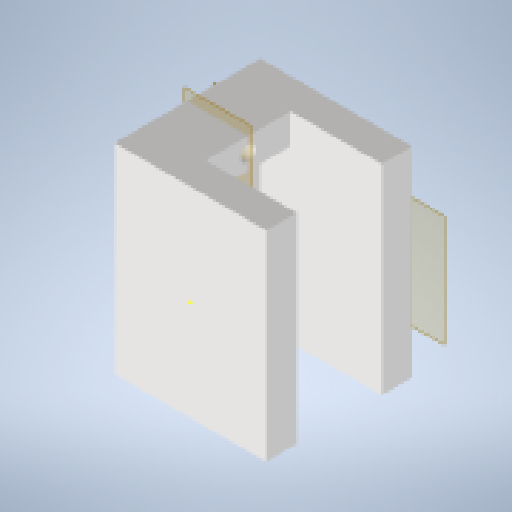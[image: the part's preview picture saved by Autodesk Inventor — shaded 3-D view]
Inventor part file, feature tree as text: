
AUTODESK INVENTOR PART (.ipt)
format: ipt  version: 2023.2 (Build 272271000, 271)  size: 275,456 bytes
history: native  units: mm
features: sketch x6, extrude x5, other x4, plane x2, mirror x1, reference x1, projected_geometry x1
ambient origin geometry x8: Origin, YZ Plane, XZ Plane, XY Plane, X Axis, Y Axis, Z Axis, Center Point
bodies: Solid1 (feature_tree)
feature tree (20):
  plane  "Work Plane1"
  extrude  "Extrusion1"  Depth=33.0mm
  extrude  "Extrusion2"  Depth=5.0mm
  extrude  "Extrusion3"  Depth=5.0mm
  sketch  "Sketch4"  dims[d8=5.0mm d9=2.5mm]
  extrude  "Extrusion4"  Depth=5.0mm
  plane  "Work Plane2"
  mirror  "Mirror1"
  extrude  "Extrusion5"  Depth=2.5mm
  sketch  "Sketch1"  dims[d0=25.0mm d1=33.0mm]
  reference  "Reference1"
  sketch  "Sketch2"  dims[d2=5.0mm d3=0.0mm d4=5.0mm]
  sketch  "Sketch3"  dims[d5=14.0mm d6=0.0mm d7=5.0mm]
  sketch  "Sketch5"  dims[d10=2.5mm d11=2.5mm]
  sketch  "Sketch6"  dims[d12=7.0mm d13=2.5mm d14=7.0mm d15=5.0mm d16=0.0mm d17=12.5mm d18=6.5mm d19=11.0mm d20=7.0mm d21=7.0mm d22=5.0mm d23=0.0mm d24=-7.0mm d25=2.0mm d26=0.0mm]
  projected_geometry  "Projected Loop1"
  other  "<userpath> windows\Documents\Inventor\Robotska_roka\Assembly4.iam"
  other  "Assembly4.iam"
  other  "SG90 - Micro Servo 9g - Tower Pro:2"
  other  "SG90 - Micro Servo 9g - Tower Pro.4"
